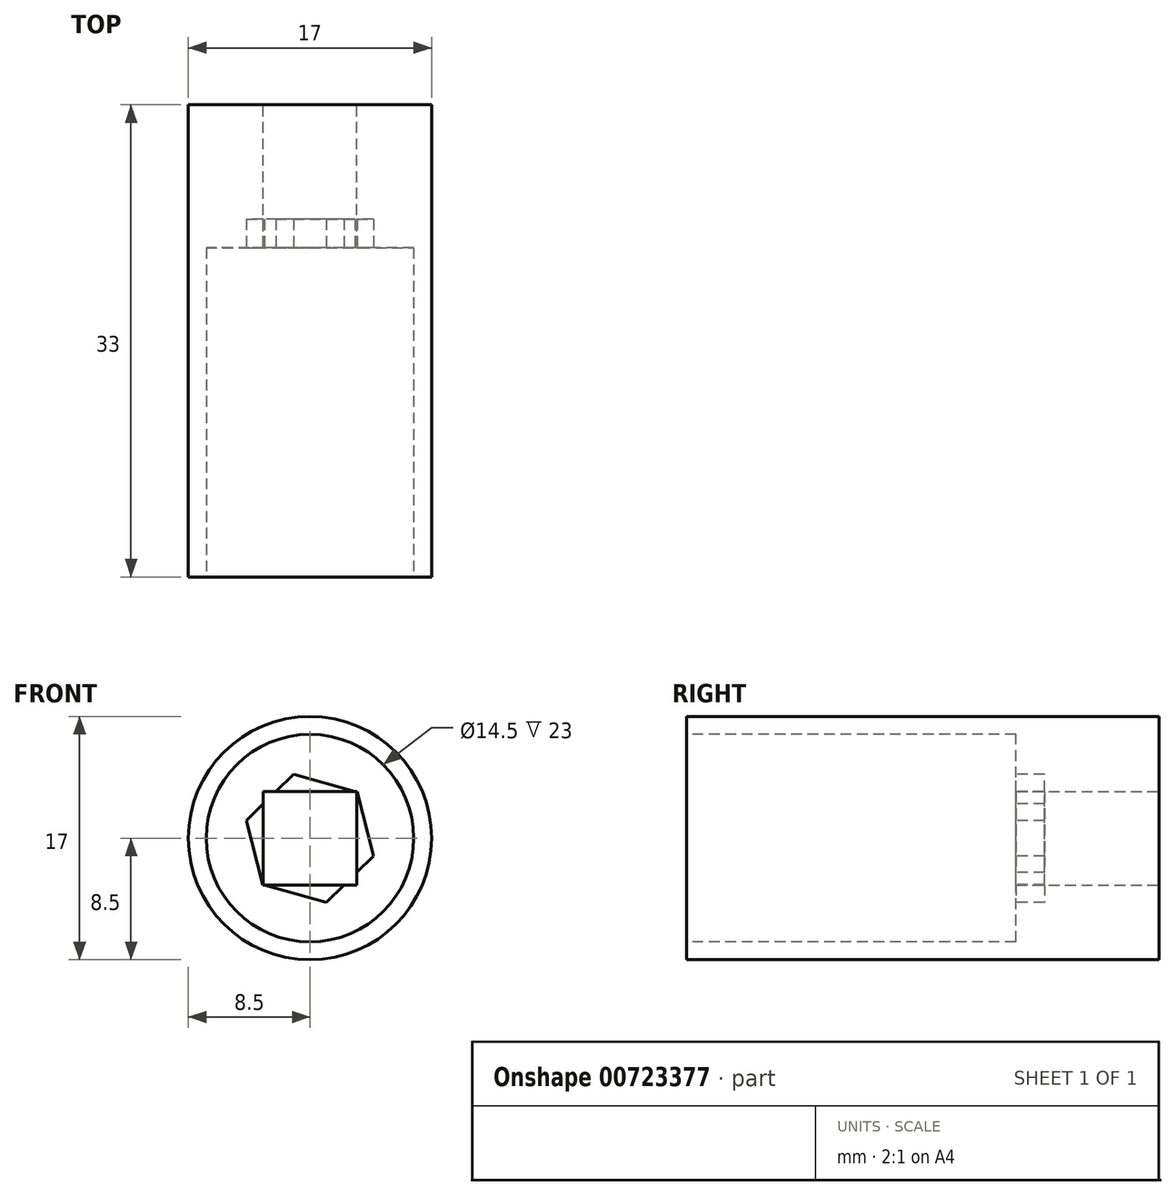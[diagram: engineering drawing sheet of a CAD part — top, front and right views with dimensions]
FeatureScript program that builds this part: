
annotation { "Feature Type Name" : "Feature", "Feature Type Description" : "" }
export const myFeature = defineFeature(function(context is Context, id is Id, definition is map)
    precondition{}
    {
        {
            var Q0;
            Q0=qCreatedBy(makeId("Front.planeOp"),FACE);
            var sketch = newSketch(context, id + "F0", { "sketchPlane" : qUnion([Q0])});
            skCircle(sketch, "E0", {"center": v(0, 0) * mm, "radius": 8.5 * mm});
            skLineSegment(sketch, "E1.bottom", {"start": v(3.28, -3.28) * mm, "end": v(-3.28, -3.28) * mm});
            skLineSegment(sketch, "E1.top", {"start": v(3.28, 3.28) * mm, "end": v(-3.27, 3.27) * mm});
            skLineSegment(sketch, "E1.left", {"start": v(3.28, -3.28) * mm, "end": v(3.28, 3.27) * mm});
            skLineSegment(sketch, "E1.right", {"start": v(-3.28, -3.28) * mm, "end": v(-3.27, 3.27) * mm});
            skSolve(sketch);
        }
        {
            var Q0;
            Q0 = qSketchRegion(id + "F0", true);
            extrude(context, id + "F1", {"entities" : qUnion([Q0]), "depth" : 33 * mm, "offsetDistance" : 25 * mm});
        }
        {
            var Q0;
            Q0=makeQuery(id+"F1.opExtrude","CAP_FACE",FACE,{"disambiguationData":[OSD([sQuery(id+"F0.wireOp",EDGE,"E0"),sQuery(id+"F0.wireOp",EDGE,"E1.bottom"),sQuery(id+"F0.wireOp",EDGE,"E1.top"),sQuery(id+"F0.wireOp",EDGE,"E1.left"),sQuery(id+"F0.wireOp",EDGE,"E1.right")])],"isStart":false});
            var sketch = newSketch(context, id + "F2", { "sketchPlane" : qUnion([Q0])});
            skCircle(sketch, "E2.cCircle", {"center": v(0, 0) * mm, "radius": 4 * mm, "construction": true});
            skLineSegment(sketch, "E2.0", {"start": v(3.3, 3.24) * mm, "end": v(4.45, -1.23) * mm});
            skLineSegment(sketch, "E2.1", {"start": v(4.45, -1.23) * mm, "end": v(1.16, -4.47) * mm});
            skLineSegment(sketch, "E2.2", {"start": v(1.16, -4.47) * mm, "end": v(-3.3, -3.24) * mm});
            skLineSegment(sketch, "E2.3", {"start": v(-3.3, -3.24) * mm, "end": v(-4.45, 1.23) * mm});
            skLineSegment(sketch, "E2.4", {"start": v(-4.45, 1.23) * mm, "end": v(-1.16, 4.47) * mm});
            skLineSegment(sketch, "E2.5", {"start": v(-1.16, 4.47) * mm, "end": v(3.3, 3.24) * mm});
            skPoint(sketch, "E2.0.midPoint", {"position": v(3.87, 1) * mm});
            skSolve(sketch);
        }
        {
            var Q0;
            {var subQ0=sQuery(id+"F2.wireOp",EDGE,"E2.3");Q0=makeQuery(id+"F2.imprint","IMPRINT",FACE,{"disambiguationData":[TD([[makeQuery(id+"F2.imprint","IMPRINT",EDGE,{"derivedFrom":subQ0}),-1.0]])]});}
            var Q1;
            {var subQ0=sQuery(id+"F2.wireOp",EDGE,"E2.2");var subQ1=sQuery(id+"F2.wireOp",EDGE,"E2.1");var subQ2=makeQuery(id+"F2.imprint","INTERSECT",VERTEX,{"derivedFrom":[subQ1,subQ0]});Q1=makeQuery(id+"F2.imprint","IMPRINT",FACE,{"disambiguationData":[TD([[makeQuery(id+"F2.imprint","IMPRINT",EDGE,{"disambiguationData":[TD([[subQ2,1.0]])],"derivedFrom":subQ1}),-1.0]])]});}
            var Q2;
            {var subQ0=sQuery(id+"F2.wireOp",EDGE,"E2.0");Q2=makeQuery(id+"F2.imprint","IMPRINT",FACE,{"disambiguationData":[TD([[makeQuery(id+"F2.imprint","IMPRINT",EDGE,{"derivedFrom":subQ0}),-1.0]])]});}
            var Q3;
            {var subQ0=sQuery(id+"F2.wireOp",EDGE,"E2.5");var subQ1=sQuery(id+"F2.wireOp",EDGE,"E2.4");var subQ2=makeQuery(id+"F2.imprint","INTERSECT",VERTEX,{"derivedFrom":[subQ1,subQ0]});Q3=makeQuery(id+"F2.imprint","IMPRINT",FACE,{"disambiguationData":[TD([[makeQuery(id+"F2.imprint","IMPRINT",EDGE,{"disambiguationData":[TD([[subQ2,1.0]])],"derivedFrom":subQ1}),-1.0]])]});}
            extrude(context, id + "F3", {"entities" : qUnion([Q0, Q1, Q2, Q3]), "operationType" : NewBodyOperationType.REMOVE, "oppositeDirection" : true, "depth" : 25 * mm, "offsetDistance" : 25 * mm});
        }
        {
            var Q0;
            Q0=makeQuery(id+"F1.opExtrude","CAP_FACE",FACE,{"disambiguationData":[OSD([sQuery(id+"F0.wireOp",EDGE,"E0"),sQuery(id+"F0.wireOp",EDGE,"E1.bottom"),sQuery(id+"F0.wireOp",EDGE,"E1.top"),sQuery(id+"F0.wireOp",EDGE,"E1.left"),sQuery(id+"F0.wireOp",EDGE,"E1.right")])],"isStart":false});
            var sketch = newSketch(context, id + "F4", { "sketchPlane" : qUnion([Q0])});
            skCircle(sketch, "E3", {"center": v(0, 0) * mm, "radius": 7.25 * mm});
            skSolve(sketch);
        }
        {
            var Q0;
            Q0=makeQuery(id+"F4.imprint","IMPRINT",FACE,{"disambiguationData":[TD([[makeQuery(id+"F4.imprint","IMPRINT",EDGE,{"derivedFrom":sQuery(id+"F4.wireOp",EDGE,"E3")}),1.0]])]});
            extrude(context, id + "F5", {"entities" : qUnion([Q0]), "operationType" : NewBodyOperationType.REMOVE, "oppositeDirection" : true, "depth" : 23 * mm, "offsetDistance" : 25 * mm});
        }
    });
